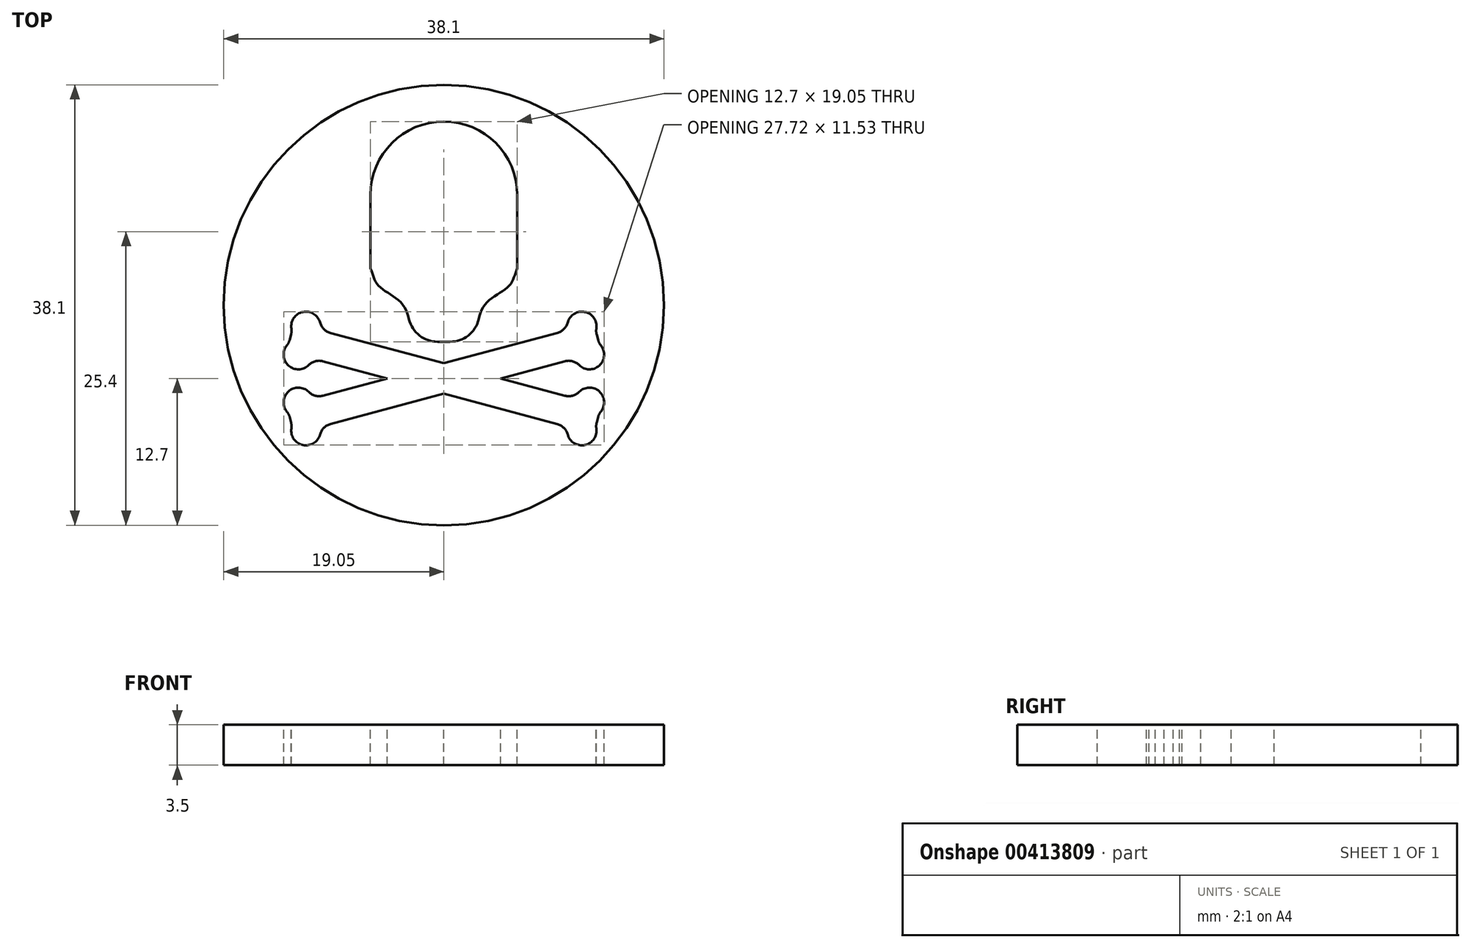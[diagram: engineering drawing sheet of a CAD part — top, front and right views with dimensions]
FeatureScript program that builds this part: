
annotation { "Feature Type Name" : "Feature", "Feature Type Description" : "" }
export const myFeature = defineFeature(function(context is Context, id is Id, definition is map)
    precondition{}
    {
        {
            var Q0;
            Q0=qCreatedBy(makeId("Top.planeOp"),FACE);
            var sketch = newSketch(context, id + "F0", { "sketchPlane" : qUnion([Q0])});
            skCircle(sketch, "E0", {"center": v(0, 0) * mm, "radius": 19.05 * mm});
            skSolve(sketch);
        }
        {
            var Q0;
            Q0 = qSketchRegion(id + "F0", true);
            extrude(context, id + "F1", {"entities" : qUnion([Q0]), "depth" : 3.5 * mm});
        }
        {
            var Q0;
            Q0=makeQuery(id+"F1.opExtrude","CAP_FACE",FACE,{"disambiguationData":[OSD([sQuery(id+"F0.wireOp",EDGE,"E0")])],"isStart":false});
            var sketch = newSketch(context, id + "F2", { "sketchPlane" : qUnion([Q0])});
            skLineSegment(sketch, "E1.bottom", {"start": v(0, 15.88) * mm, "end": v(0, 15.88) * mm});
            skLineSegment(sketch, "E1.top", {"start": v(0.54, -3.18) * mm, "end": v(-0.54, -3.18) * mm});
            skLineSegment(sketch, "E1.left", {"start": v(6.35, 9.52) * mm, "end": v(6.35, 3.18) * mm});
            skLineSegment(sketch, "E1.right", {"start": v(-6.35, 9.52) * mm, "end": v(-6.35, 3.17) * mm});
            skPoint(sketch, "E1.middle", {"position": v(0, 6.35) * mm});
            skPoint(sketch, "E2.visualSharp", {"position": v(-6.35, 15.88) * mm});
            skArc(sketch, "E2.filletArc", {"start": v(0, 15.88) * mm, "mid": v(-4.5, 14.02) * mm, "end": v(-6.35, 9.52) * mm});
            skPoint(sketch, "E3.visualSharp", {"position": v(6.35, 15.88) * mm});
            skArc(sketch, "E3.filletArc", {"start": v(6.35, 9.52) * mm, "mid": v(4.5, 14.02) * mm, "end": v(0, 15.88) * mm});
            skFitSpline(sketch, "E4", {"points": [v(-6.35, 3.17) * mm, v(-5.66, 1.69) * mm, v(-3.53, 0) * mm, v(-2.54, -3.18) * mm], "startDerivative": vector(2.39, -5.8) * mm, "endDerivative": vector(3.14, -8.85) * mm});
            skLineSegment(sketch, "E5", {"start": v(0, 15.88) * mm, "end": v(0, -3.18) * mm});
            skFitSpline(sketch, "E6.MirrorCS", {"points": [v(6.35, 3.17) * mm, v(5.66, 1.69) * mm, v(3.53, 0) * mm, v(2.54, -3.17) * mm], "startDerivative": vector(-2.39, -5.8) * mm, "endDerivative": vector(-3.14, -8.85) * mm});
            skPoint(sketch, "E7.orphan", {"position": v(-6.35, -3.17) * mm});
            skPoint(sketch, "E8.orphan", {"position": v(6.35, -3.18) * mm});
            skArc(sketch, "E9.filletArc", {"start": v(-3.01, -1.24) * mm, "mid": v(-2.11, -2.63) * mm, "end": v(-0.54, -3.17) * mm});
            skPoint(sketch, "E10.visualSharp", {"position": v(2.54, -3.18) * mm});
            skArc(sketch, "E10.filletArc", {"start": v(0.54, -3.17) * mm, "mid": v(2.11, -2.63) * mm, "end": v(3.01, -1.24) * mm});
            skSolve(sketch);
        }
        {
            var Q0;
            Q0 = qSketchRegion(id + "F2", true);
            extrude(context, id + "F3", {"entities" : qUnion([Q0]), "operationType" : NewBodyOperationType.REMOVE, "oppositeDirection" : true, "depth" : 5.33 * mm});
        }
        {
            var Q0;
            Q0=makeQuery(id+"F1.opExtrude","CAP_FACE",FACE,{"disambiguationData":[OSD([sQuery(id+"F0.wireOp",EDGE,"E0")])],"isStart":false});
            var sketch = newSketch(context, id + "F4", { "sketchPlane" : qUnion([Q0])});
            skLineSegment(sketch, "E11", {"start": v(-11.94, -1.84) * mm, "end": v(12.6, -8.41) * mm});
            skLineSegment(sketch, "E12", {"start": v(12.6, -8.41) * mm, "end": v(11.94, -10.86) * mm});
            skLineSegment(sketch, "E13", {"start": v(11.94, -10.86) * mm, "end": v(-12.6, -4.29) * mm});
            skLineSegment(sketch, "E14", {"start": v(-12.6, -4.29) * mm, "end": v(-11.94, -1.84) * mm});
            skLineSegment(sketch, "E15", {"start": v(-12.27, -3.06) * mm, "end": v(12.27, -9.64) * mm});
            skPoint(sketch, "E16", {"position": v(0, -6.35) * mm});
            skLineSegment(sketch, "E17", {"start": v(-12.6, -8.41) * mm, "end": v(9.81, -2.4) * mm});
            skLineSegment(sketch, "E18", {"start": v(11.94, -1.84) * mm, "end": v(12.6, -4.29) * mm});
            skLineSegment(sketch, "E19", {"start": v(10.47, -4.86) * mm, "end": v(-11.94, -10.86) * mm});
            skLineSegment(sketch, "E20", {"start": v(-11.94, -10.86) * mm, "end": v(-12.6, -8.41) * mm});
            skLineSegment(sketch, "E21", {"start": v(-12.27, -9.64) * mm, "end": v(12.27, -3.06) * mm});
            skLineSegment(sketch, "E22", {"start": v(0, 0) * mm, "end": v(0, -6.35) * mm});
            skArc(sketch, "E23", {"start": v(13.2, -2.03) * mm, "mid": v(12.2, -0.6) * mm, "end": v(10.71, -1.5) * mm});
            skArc(sketch, "E24", {"start": v(11.7, -5.19) * mm, "mid": v(13.44, -5.24) * mm, "end": v(13.59, -3.5) * mm});
            skLineSegment(sketch, "E25", {"start": v(13.22, -2.55) * mm, "end": v(13.35, -3.03) * mm});
            skPoint(sketch, "E26.visualSharp", {"position": v(13.14, -2.24) * mm});
            skArc(sketch, "E26.filletArc", {"start": v(13.2, -2.03) * mm, "mid": v(13.18, -2.3) * mm, "end": v(13.22, -2.55) * mm});
            skPoint(sketch, "E27.visualSharp", {"position": v(13.43, -3.33) * mm});
            skArc(sketch, "E27.filletArc", {"start": v(13.35, -3.03) * mm, "mid": v(13.45, -3.28) * mm, "end": v(13.59, -3.5) * mm});
            skPoint(sketch, "E28.visualSharp", {"position": v(10.71, -2.16) * mm});
            skArc(sketch, "E28.filletArc", {"start": v(9.81, -2.4) * mm, "mid": v(10.38, -2.08) * mm, "end": v(10.71, -1.5) * mm});
            skPoint(sketch, "E29.visualSharp", {"position": v(11.37, -4.62) * mm});
            skArc(sketch, "E29.filletArc", {"start": v(11.7, -5.19) * mm, "mid": v(11.13, -4.86) * mm, "end": v(10.47, -4.86) * mm});
            skLineSegment(sketch, "E30", {"start": v(0, -6.35) * mm, "end": v(13.76, -6.35) * mm});
            skArc(sketch, "E31.MirrorCS", {"start": v(11.7, -7.51) * mm, "mid": v(11.13, -7.84) * mm, "end": v(10.47, -7.84) * mm});
            skArc(sketch, "E32.MirrorCS", {"start": v(11.7, -7.51) * mm, "mid": v(13.44, -7.46) * mm, "end": v(13.59, -9.2) * mm});
            skArc(sketch, "E33.MirrorCS", {"start": v(13.35, -9.67) * mm, "mid": v(13.45, -9.42) * mm, "end": v(13.59, -9.2) * mm});
            skLineSegment(sketch, "E34.MirrorCS", {"start": v(13.22, -10.15) * mm, "end": v(13.35, -9.67) * mm});
            skArc(sketch, "E35.MirrorCS", {"start": v(13.2, -10.67) * mm, "mid": v(13.18, -10.4) * mm, "end": v(13.22, -10.15) * mm});
            skArc(sketch, "E36.MirrorCS", {"start": v(13.2, -10.67) * mm, "mid": v(12.2, -12.1) * mm, "end": v(10.71, -11.2) * mm});
            skArc(sketch, "E37.MirrorCS", {"start": v(9.81, -10.3) * mm, "mid": v(10.38, -10.62) * mm, "end": v(10.71, -11.2) * mm});
            skArc(sketch, "E38.MirrorCS", {"start": v(-13.2, -2.03) * mm, "mid": v(-12.2, -0.6) * mm, "end": v(-10.71, -1.5) * mm});
            skArc(sketch, "E39.MirrorCS", {"start": v(-9.81, -2.4) * mm, "mid": v(-10.38, -2.08) * mm, "end": v(-10.71, -1.5) * mm});
            skArc(sketch, "E40.MirrorCS", {"start": v(-11.7, -5.19) * mm, "mid": v(-13.44, -5.24) * mm, "end": v(-13.59, -3.5) * mm});
            skArc(sketch, "E41.MirrorCS", {"start": v(-11.7, -5.19) * mm, "mid": v(-11.13, -4.86) * mm, "end": v(-10.47, -4.86) * mm});
            skArc(sketch, "E42.MirrorCS", {"start": v(-13.35, -3.03) * mm, "mid": v(-13.45, -3.28) * mm, "end": v(-13.59, -3.5) * mm});
            skLineSegment(sketch, "E43.MirrorCS", {"start": v(-13.22, -2.55) * mm, "end": v(-13.35, -3.03) * mm});
            skArc(sketch, "E44.MirrorCS", {"start": v(-13.2, -2.03) * mm, "mid": v(-13.18, -2.3) * mm, "end": v(-13.22, -2.55) * mm});
            skArc(sketch, "E45.MirrorCS", {"start": v(-11.7, -7.51) * mm, "mid": v(-11.13, -7.84) * mm, "end": v(-10.47, -7.84) * mm});
            skArc(sketch, "E46.MirrorCS", {"start": v(-11.7, -7.51) * mm, "mid": v(-13.44, -7.46) * mm, "end": v(-13.59, -9.2) * mm});
            skArc(sketch, "E47.MirrorCS", {"start": v(-13.35, -9.67) * mm, "mid": v(-13.45, -9.42) * mm, "end": v(-13.59, -9.2) * mm});
            skLineSegment(sketch, "E48.MirrorCS", {"start": v(-13.22, -10.15) * mm, "end": v(-13.35, -9.67) * mm});
            skArc(sketch, "E49.MirrorCS", {"start": v(-13.2, -10.67) * mm, "mid": v(-13.18, -10.4) * mm, "end": v(-13.22, -10.15) * mm});
            skArc(sketch, "E50.MirrorCS", {"start": v(-13.2, -10.67) * mm, "mid": v(-12.2, -12.1) * mm, "end": v(-10.71, -11.2) * mm});
            skArc(sketch, "E51.MirrorCS", {"start": v(-9.81, -10.3) * mm, "mid": v(-10.38, -10.62) * mm, "end": v(-10.71, -11.2) * mm});
            skSolve(sketch);
        }
        {
            var Q0;
            Q0 = qSketchRegion(id + "F4", true);
            var Q1;
            {var subQ0=sQuery(id+"F4.wireOp",EDGE,"79daabfb-e708-4f8d-b930-0284830156720.MirrorCS");Q1=makeQuery(id+"F4.imprint","IMPRINT",FACE,{"disambiguationData":[TD([[makeQuery(id+"F4.imprint","IMPRINT",EDGE,{"derivedFrom":subQ0}),-1.0]])]});}
            var Q2;
            {var subQ0=sQuery(id+"F4.wireOp",EDGE,"81815b4a-eb9a-46ba-bb84-2da79c74dedf0.MirrorCS");Q2=makeQuery(id+"F4.imprint","IMPRINT",FACE,{"disambiguationData":[TD([[makeQuery(id+"F4.imprint","IMPRINT",EDGE,{"derivedFrom":subQ0}),-1.0]])]});}
            var Q3;
            {var subQ0=sQuery(id+"F4.wireOp",EDGE,"f94ec01d-3a1b-4ee6-b849-c2fed6d013ab0.MirrorCS");var subQ1=sQuery(id+"F4.wireOp",EDGE,"nyevlk8L-7Z2X-lH10-pc4Y-s9fzSUyXAaBk");var subQ2=makeQuery(id+"F4.imprint","INTERSECT",VERTEX,{"derivedFrom":[subQ1,subQ0]});Q3=makeQuery(id+"F4.imprint","IMPRINT",FACE,{"disambiguationData":[TD([[makeQuery(id+"F4.imprint","IMPRINT",EDGE,{"disambiguationData":[TD([[subQ2,1.0]])],"derivedFrom":subQ1}),-1.0]])]});}
            var Q4;
            {var subQ0=sQuery(id+"F4.wireOp",EDGE,"6840b8d1-15e5-4749-b6c6-1a15b524e8780.MirrorCS");var subQ1=sQuery(id+"F4.wireOp",EDGE,"PieO4w4A-Decb-AyKF-tgIh-CT2OS44ABLdv");var subQ2=makeQuery(id+"F4.imprint","INTERSECT",VERTEX,{"derivedFrom":[subQ1,subQ0]});Q4=makeQuery(id+"F4.imprint","IMPRINT",FACE,{"disambiguationData":[TD([[makeQuery(id+"F4.imprint","IMPRINT",EDGE,{"disambiguationData":[TD([[subQ2,1.0]])],"derivedFrom":subQ1}),-1.0]])]});}
            extrude(context, id + "F5", {"entities" : qUnion([Q0, Q1, Q2, Q3, Q4]), "operationType" : NewBodyOperationType.REMOVE, "oppositeDirection" : true, "depth" : 25.4 * mm});
        }
    });
